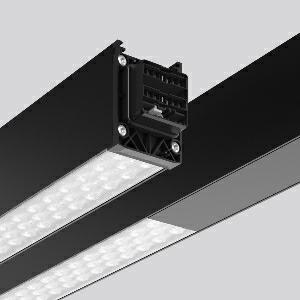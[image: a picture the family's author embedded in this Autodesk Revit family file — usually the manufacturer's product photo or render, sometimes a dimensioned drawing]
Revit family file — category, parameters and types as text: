
# Revit family: linedo_4_5m_30_11001100_954530_843_476_500_bbee
name_source: partatom
category: Lighting Fixtures
units: mm (PartAtom-declared; Revit-internal decimal feet)

## family parameters
Cut with Voids When Loaded = No
Host = Face
Light Source = No
Part Type = Normal
Room Calculation Point = No
Round Connector Dimension = Use Diameter
Shared = No

## types (1)
- LINEDO_4,5m_30_11001100 (1 x LED Modul 840, 1700 lm, 4000)
    Apparent Load = 40 VA
    CIE Flux Codes = 89 97 99 100 100
    Color Rendering = 80
    Color Temperature = 4000
    Default Elevation = 1800 mm
    Description = LINEDO, 40 W, 6800 lm, 840, black, DALI
Continuous line luminaire, L 4547 B 58 H 76
    Height = 76 mm
    Lamp = 1 x LED Modul 840
    Lamp Light Flux = 1700 lm
    Lamp count = 1
    Length = 4547 mm
    Lifetime = 50000 h
    Luminous efficacy = 170 lm/W
    Manufacturer = RZB
    ModVariant = No
    Model = 954530.843.476.500
    Mounting Place = Ceiling
    Mounting Type = Surface mounted, Pendant
    Number of Poles = 1
    OnlyDefault = Yes
    Power Factor = 1
    Product Name = LINEDO_4,5m_30_11001100
    Product group = Surface mounted continuous line luminaire system
    ProductGroupID = 310
    Protection Class = Protection class I
    Protection Degree = IP 54
    RLX_Detail_Level = 1
    RLX_Emergency_Light_Flux = 0 lm
    RLX_Emergency_Type = 0
    RLX_Emergency_Type_DB = No
    RlxData = <blob elided: 56829 chars, md5=5f47b399>
    Socket = socket
    Standby Power = 0 W
    System Light Flux = 6800 lm
    System Power = 40 W
    Type Comments = Product without accessories
    Type Image = 954530.853.476.504.jpg
    URL = http://relux.com
    VarID = ---
    Voltage = 230 V
    Voltage Range = 220-240 V
    Weight = 0.00 kg
    Width = 58 mm

## geometry (parser evidence)
native form markers: Blend x4, Sweep x21
no freeform markers — native parametric forms only
